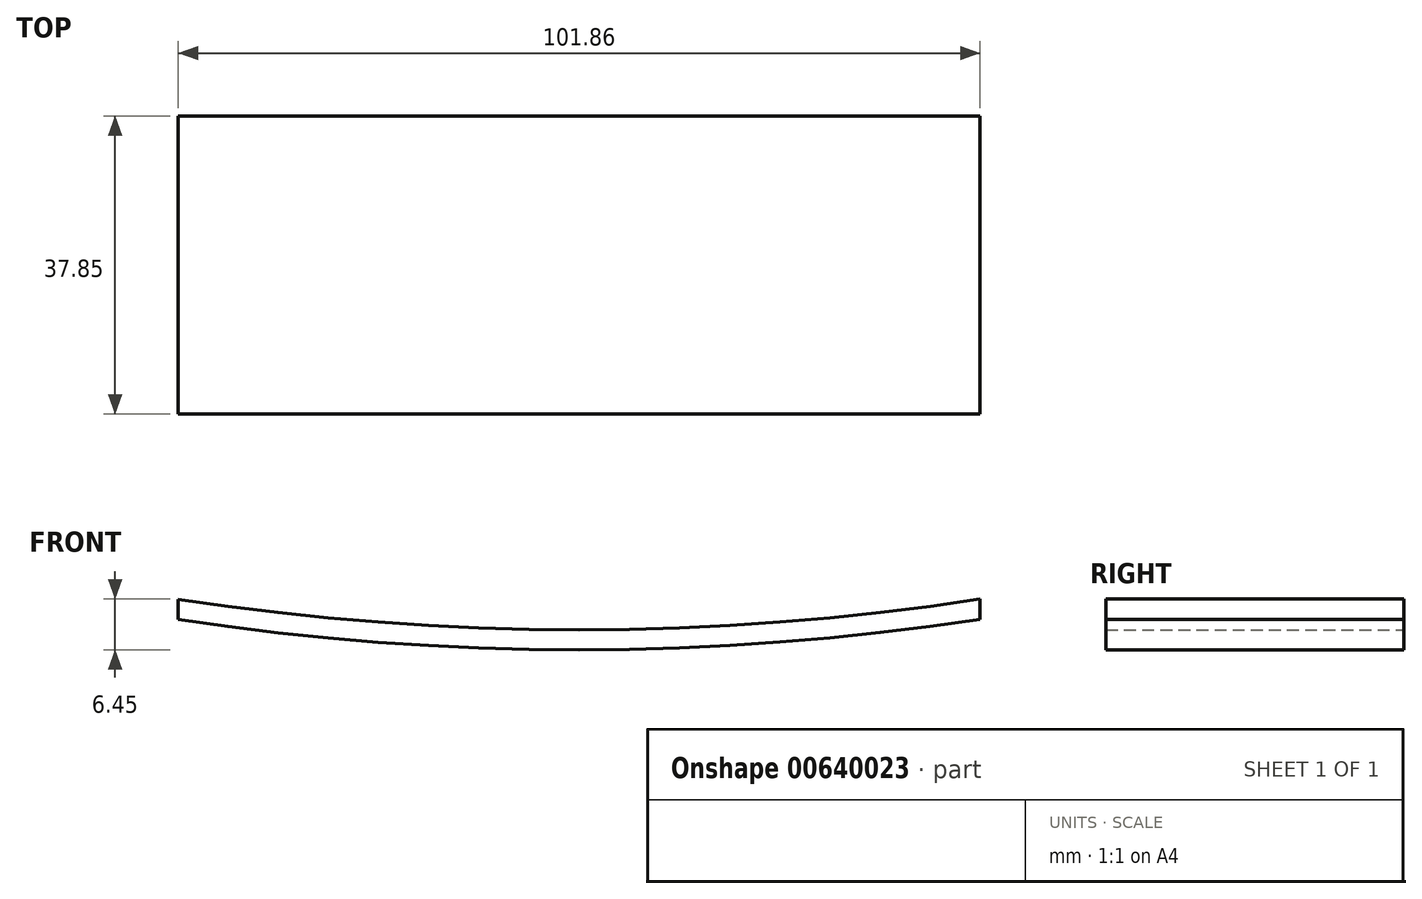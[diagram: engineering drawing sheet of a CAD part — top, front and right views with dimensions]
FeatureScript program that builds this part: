
annotation { "Feature Type Name" : "Feature", "Feature Type Description" : "" }
export const myFeature = defineFeature(function(context is Context, id is Id, definition is map)
    precondition{}
    {
        {
            var Q0;
            Q0=qCreatedBy(makeId("Front.planeOp"),FACE);
            var sketch = newSketch(context, id + "F0", { "sketchPlane" : qUnion([Q0])});
            skArc(sketch, "E0", {"start": v(-88.15, -323.38) * mm, "mid": v(-37.22, -327.27) * mm, "end": v(13.7, -323.36) * mm});
            skArc(sketch, "E1", {"start": v(-88.15, -325.95) * mm, "mid": v(-37.22, -329.8) * mm, "end": v(13.7, -325.93) * mm});
            skPoint(sketch, "E2", {"position": v(-37.3, -327.27) * mm});
            skPoint(sketch, "E3", {"position": v(13.7, -323.36) * mm});
            skPoint(sketch, "E4", {"position": v(-88.15, -323.38) * mm});
            skLineSegment(sketch, "E5", {"start": v(-88.15, -323.38) * mm, "end": v(-88.15, -325.95) * mm});
            skLineSegment(sketch, "E6", {"start": v(13.7, -323.36) * mm, "end": v(13.7, -325.93) * mm});
            skSolve(sketch);
        }
        {
            var Q0;
            Q0 = qSketchRegion(id + "F0", true);
            extrude(context, id + "F1", {"entities" : qUnion([Q0]), "depth" : 37.85 * mm, "offsetDistance" : 25.4 * mm});
        }
    });
